# Revit family: SRT2-Yoke Mount
name_source: partatom
category: Lighting Fixtures
units: mm (PartAtom-declared; Revit-internal decimal feet)

## family parameters
Cut with Voids When Loaded = No
Host = Face
Light Source = Yes
OmniClass Number = 23.80.70.11.14.11
OmniClass Title = Downlights
Part Type = Normal
Room Calculation Point = No
Round Connector Dimension = Use Diameter
Shared = No

## types (1)
- SRT2
    Apparent Load = 140 VA
    Ballast = Paint - Carbon Black
    Certifications = • Listed to UL1598 for use in wet location,
listed for -40o
C to 40o
C applications
• IDA approved with zero uplight for 3000K
and warmer CCTs
• IP65
    Color Filter = 16777215
    Cord Height = 17.5 "
    Default Elevation = 48 "
    Description = Large Edge-Lit luminaire, the ideal solution for parking garage and canopy applications. Provides exceptional visual comfort and photometric performance in sleek low profile housing. Available in a wide range of lumen outputs and photometric distributions paired with a specially designed lens for optimal visual comfort and performance. Control options available for site customization and additional energy savings.
    Dimming Lamp Color Temperature Shift = <None>
    Emit Shape Visible in Rendering = No
    Emit from Circle Diameter = 4 "
    Features = •	Size measuring 18.5 inch x 4.0 inch
•	Visual comfort Edge-Lit design
•	4,000-16,000 lumens
•	Option uplight module provides 800 lumens of indirect illumination
•	Surface, pendant and trunnion mounting options
•	Control options including occupancy sensing, NX Distributed Intelligence™, wiSCAPE®
•	Battery backup and UL 924 control options
•	Optional bird shield and vandal deterring wire guard
    Lamp = LED Lamp
    Manufacturer = Beacon Products
    Model = SRT2
    Photometric Web File = generic.ies
    Reflector = Glass
    Tilt Angle = -90.00°
    URL = https://www.currentlighting.com
    Voltage = 120 V
    Warranty = • 5 year warranty
• See HLI Standard Warranty for
additional information
    Wattage Comments = 30-140W

## geometry (parser evidence)
native form markers: Blend x2, Sweep x4
no freeform markers — native parametric forms only
